# Revit family: 22-90001024-25_BIM File
name_source: partatom
category: Pipe Accessories
units: mm (PartAtom-declared; Revit-internal decimal feet)

## family parameters
Cut with Voids When Loaded = No
Host = Face
Part Type = Normal
Round Connector Dimension = Use Diameter
Shared = No

## types (3) — shared parameters
AssetIdentifier = Please Record On Commissioning.
AssetType = Fixed
BarCode = Please Record On Commissioning.
ClassificationName = Uniclass2015
ClassificationValue = Pr_65_52_61_15
Color = Metal
DocumentationInstallationGuide = https://www.airflow.com
DocumentationTechnical = https://www.airflow.com
DurationUnit = Year
Export Type to IFC As = IfcBuildingElementProxyType
Finish = Galvanised Steel
IfcExportAs = IfcBuildingElementProxyType
IfcExportType = USERDEFINED
InstallationDate = Please Record On Commissioning.
IntumescentMaterial = Airflow - Intumescent Material
Manufacturer = Airflow
ManufacturerName = Airflow
Material = Intumescent
NBSDescription = Pipe sleeves
NBSReference = 90-10-60/405
ProductionYear = 2019
ReferencedStandard = Tested to BSEN 1366-3: 2009 Classified according to EN 13501-2: 2007 + A1: 2009
ReplacementCost = 0
SerialNumber = Please Record On Commissioning.
ShellMaterial = Airflow - Galvanised Steel
Type IFC Predefined Type = USERDEFINED
WarrantyDurationLabor = 0
WarrantyDurationParts = 0
WarrantyDurationUnit = Year
WarrantyStartDate = Please Record On Commissioning.
_BSBibleVersion = 16
_CurrentRevision = 1
_DistributedBy = Airflow
zero-valued in all types: Default Elevation, ExpectedLife, _BimSpecGuid

## per-type parameters (varying)
- 90001022: ApertureHeight=97 mm  [stored 0.318241 ft]; ApertureRadius=48.5 mm  [stored 0.159121 ft]; ApertureWidth=97 mm  [stored 0.318241 ft]; BIMObjectName=90001022_BIM File; C_Length=140 mm  [stored 0.459318 ft]; C_Offset=0 mm  [stored 0 ft]; Circular=Yes; Description=Fire Sleeve 75mm Diameter Double Ended; DuctHeight=75 mm; DuctRadius=37.5 mm; DuctSize=Ø 75mm; DuctWidth=75 mm; FireRating=120 minutes; InnerSleeveRadius=46 mm; Length=140 mm  [stored 0.459318 ft]; ModelReference=Vent Duct Fire Sleeve; NBSObjectName=75mm Double Ended Fire Sleeve; NominalDepth=95 mm; NominalHeight=95 mm; NominalLength=140 mm  [stored 0.459318 ft]; OuterSleeveRadius=47.5 mm; R_Length=5 mm  [stored 0.0164042 ft]; R_Offset=20 mm  [stored 0.0656168 ft]; Rectangular=No; Shape=Cylindrical; Size=Ø95mm x 140mm; SpaceRequired=10 mm  [stored 0.0328084 ft]; Type Comments=Vent Duct Fire Sleeve; TypeName=Vent Duct Fire Sleeve; URL=https://www.airflow.com
- 90001024: ApertureHeight=170 mm  [stored 0.557743 ft]; ApertureRadius=85 mm  [stored 0.278871 ft]; ApertureWidth=170 mm  [stored 0.557743 ft]; BIMObjectName=90001024_BIM File; C_Length=180 mm  [stored 0.590551 ft]; C_Offset=0 mm  [stored 0 ft]; Circular=Yes; Description=Fire Sleeve 125mm Diameter Double Ended; DuctHeight=125 mm  [stored 0.410105 ft]; DuctRadius=62.5 mm  [stored 0.205052 ft]; DuctSize=Ø 125mm; DuctWidth=125 mm  [stored 0.410105 ft]; FireRating=90 minutes; InnerSleeveRadius=81 mm; Keynote=Z12; Length=180 mm  [stored 0.590551 ft]; ModelReference=Duct Fire Sleeve; NBSObjectName=Airflow - Pipe sleeves; NominalDepth=165 mm; NominalHeight=165 mm; NominalLength=180 mm  [stored 0.590551 ft]; OuterSleeveRadius=82.5 mm; R_Length=5 mm  [stored 0.0164042 ft]; R_Offset=20 mm  [stored 0.0656168 ft]; Rectangular=No; Shape=Cylindrical; Size=Ø165mm x 180mm; SpaceRequired=20 mm  [stored 0.0656168 ft]; Type Comments=Duct Fire Sleeve; TypeName=Duct Fire Sleeve; URL=https://www.airflow.com
- 90001025: ApertureHeight=80 mm  [stored 0.262467 ft]; ApertureRadius=112.5 mm  [stored 0.369094 ft]; ApertureWidth=225 mm  [stored 0.738189 ft]; BIMObjectName=90001025_BIM File; C_Length=5 mm  [stored 0.0164042 ft]; C_Offset=20 mm  [stored 0.0656168 ft]; Circular=No; Description=205x 60 Rectangular Double Ended Fire Sleeve; DuctHeight=60 mm  [stored 0.19685 ft]; DuctRadius=102.5 mm  [stored 0.336286 ft]; DuctSize=205 x 60mm; DuctWidth=205 mm  [stored 0.672572 ft]; FireRating=120 minutes; InnerSleeveRadius=110 mm  [stored 0.360892 ft]; Keynote=Z12; Length=180 mm  [stored 0.590551 ft]; ModelReference=Vent Duct Fire Sleeve; NBSObjectName=Airflow - Pipe sleeves; NominalDepth=223 mm  [stored 0.731627 ft]; NominalHeight=78 mm  [stored 0.255906 ft]; NominalLength=180 mm  [stored 0.590551 ft]; OuterSleeveRadius=111.5 mm  [stored 0.365814 ft]; R_Length=180 mm  [stored 0.590551 ft]; R_Offset=0 mm  [stored 0 ft]; Rectangular=Yes; Shape=Rectangular; Size=230mm x 85mm x 180mm; SpaceRequired=9 mm  [stored 0.0295276 ft]; Type Comments=Vent Duct Fire Sleeve; TypeName=Vent Duct Fire Sleeve; URL=https://www.airflow.co.uk

note: column(s) folded — value = type name in every type: Model

note: [stored X ft] marks values corroborated as IEEE doubles in the binary element streams (Revit-internal decimal feet)

## geometry (parser evidence)
native form markers: Sweep x1
no freeform markers — native parametric forms only
